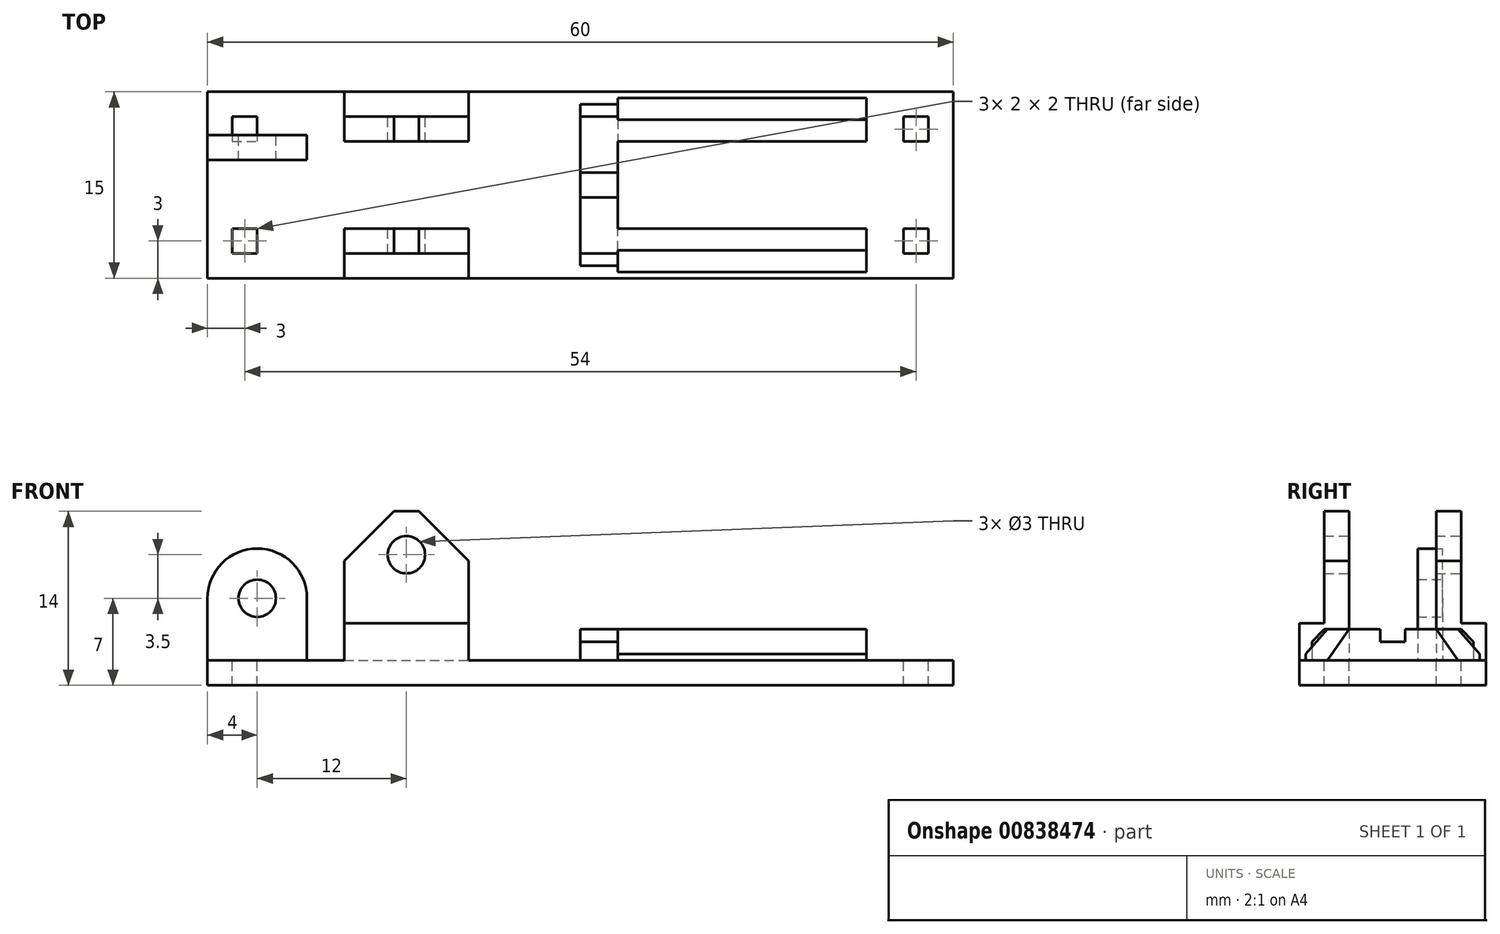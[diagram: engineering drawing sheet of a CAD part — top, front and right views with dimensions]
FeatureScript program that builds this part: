
annotation { "Feature Type Name" : "Feature", "Feature Type Description" : "" }
export const myFeature = defineFeature(function(context is Context, id is Id, definition is map)
    precondition{}
    {
        {
            var Q0;
            Q0=qCreatedBy(makeId("Top.planeOp"),FACE);
            var sketch = newSketch(context, id + "F0", { "sketchPlane" : qUnion([Q0])});
            skLineSegment(sketch, "E0.bottom", {"start": v(-30, -7.5) * mm, "end": v(30, -7.5) * mm});
            skLineSegment(sketch, "E0.top", {"start": v(-30, 7.5) * mm, "end": v(30, 7.5) * mm});
            skLineSegment(sketch, "E0.left", {"start": v(-30, -7.5) * mm, "end": v(-30, 7.5) * mm});
            skLineSegment(sketch, "E0.right", {"start": v(30, -7.5) * mm, "end": v(30, 7.5) * mm});
            skPoint(sketch, "E0.middle", {"position": v(0, 0) * mm});
            skLineSegment(sketch, "E1.bottom", {"start": v(-28, 5.5) * mm, "end": v(-26, 5.5) * mm});
            skLineSegment(sketch, "E1.top", {"start": v(-28, 3.5) * mm, "end": v(-26, 3.5) * mm});
            skLineSegment(sketch, "E1.left", {"start": v(-28, 5.5) * mm, "end": v(-28, 3.5) * mm});
            skLineSegment(sketch, "E1.right", {"start": v(-26, 5.5) * mm, "end": v(-26, 3.5) * mm});
            skLineSegment(sketch, "E2.bottom", {"start": v(-28, -3.5) * mm, "end": v(-26, -3.5) * mm});
            skLineSegment(sketch, "E2.top", {"start": v(-28, -5.5) * mm, "end": v(-26, -5.5) * mm});
            skLineSegment(sketch, "E2.left", {"start": v(-28, -3.5) * mm, "end": v(-28, -5.5) * mm});
            skLineSegment(sketch, "E2.right", {"start": v(-26, -3.5) * mm, "end": v(-26, -5.5) * mm});
            skLineSegment(sketch, "E3.bottom", {"start": v(26, -3.5) * mm, "end": v(28, -3.5) * mm});
            skLineSegment(sketch, "E3.top", {"start": v(26, -5.5) * mm, "end": v(28, -5.5) * mm});
            skLineSegment(sketch, "E3.left", {"start": v(26, -3.5) * mm, "end": v(26, -5.5) * mm});
            skLineSegment(sketch, "E3.right", {"start": v(28, -3.5) * mm, "end": v(28, -5.5) * mm});
            skLineSegment(sketch, "E4.bottom", {"start": v(26, 3.5) * mm, "end": v(28, 3.5) * mm});
            skLineSegment(sketch, "E4.top", {"start": v(26, 5.5) * mm, "end": v(28, 5.5) * mm});
            skLineSegment(sketch, "E4.left", {"start": v(26, 3.5) * mm, "end": v(26, 5.5) * mm});
            skLineSegment(sketch, "E4.right", {"start": v(28, 3.5) * mm, "end": v(28, 5.5) * mm});
            skLineSegment(sketch, "E5.bottom", {"start": v(-19, 5.5) * mm, "end": v(-9, 5.5) * mm});
            skLineSegment(sketch, "E5.top", {"start": v(-19, 3.5) * mm, "end": v(-9, 3.5) * mm});
            skLineSegment(sketch, "E5.left", {"start": v(-19, 5.5) * mm, "end": v(-19, 3.5) * mm});
            skLineSegment(sketch, "E5.right", {"start": v(-9, 5.5) * mm, "end": v(-9, 3.5) * mm});
            skLineSegment(sketch, "E6.bottom", {"start": v(-19, -3.5) * mm, "end": v(-9, -3.5) * mm});
            skLineSegment(sketch, "E6.top", {"start": v(-19, -5.5) * mm, "end": v(-9, -5.5) * mm});
            skLineSegment(sketch, "E6.left", {"start": v(-19, -3.5) * mm, "end": v(-19, -5.5) * mm});
            skLineSegment(sketch, "E6.right", {"start": v(-9, -3.5) * mm, "end": v(-9, -5.5) * mm});
            skLineSegment(sketch, "E7", {"start": v(-9, -5.5) * mm, "end": v(-9, -7.5) * mm});
            skLineSegment(sketch, "E8", {"start": v(-19, -5.5) * mm, "end": v(-19, -7.5) * mm});
            skLineSegment(sketch, "E9", {"start": v(-19, 5.5) * mm, "end": v(-19, 7.5) * mm});
            skLineSegment(sketch, "E10", {"start": v(-9, 5.5) * mm, "end": v(-9, 7.5) * mm});
            skLineSegment(sketch, "E11.bottom", {"start": v(3, -3.5) * mm, "end": v(23, -3.5) * mm});
            skLineSegment(sketch, "E11.top", {"start": v(3, -7) * mm, "end": v(23, -7) * mm});
            skLineSegment(sketch, "E11.left", {"start": v(3, -3.5) * mm, "end": v(3, -7) * mm});
            skLineSegment(sketch, "E11.right", {"start": v(23, -3.5) * mm, "end": v(23, -7) * mm});
            skLineSegment(sketch, "E12.bottom", {"start": v(3, 7) * mm, "end": v(23, 7) * mm});
            skLineSegment(sketch, "E12.top", {"start": v(3, 3.5) * mm, "end": v(23, 3.5) * mm});
            skLineSegment(sketch, "E12.left", {"start": v(3, 7) * mm, "end": v(3, 3.5) * mm});
            skLineSegment(sketch, "E12.right", {"start": v(23, 7) * mm, "end": v(23, 3.5) * mm});
            skLineSegment(sketch, "E13.bottom", {"start": v(3, 6.5) * mm, "end": v(0, 6.5) * mm});
            skLineSegment(sketch, "E13.top", {"start": v(3, -6.5) * mm, "end": v(0, -6.5) * mm});
            skLineSegment(sketch, "E13.left", {"start": v(3, 6.5) * mm, "end": v(3, -6.5) * mm});
            skLineSegment(sketch, "E13.right", {"start": v(0, 6.5) * mm, "end": v(0, -6.5) * mm});
            skSolve(sketch);
        }
        {
            var Q0;
            {var subQ0=sQuery(id+"F0.wireOp",EDGE,"E0.left");Q0=qUnion([makeQuery(id+"F0.imprint","IMPRINT",FACE,{"disambiguationData":[TD([[makeQuery(id+"F0.imprint","IMPRINT",EDGE,{"derivedFrom":sQuery(id+"F0.wireOp",EDGE,"E6.top")}),-1.0]])]}),makeQuery(id+"F0.imprint","IMPRINT",FACE,{"disambiguationData":[TD([[makeQuery(id+"F0.imprint","IMPRINT",EDGE,{"derivedFrom":sQuery(id+"F0.wireOp",EDGE,"E5.bottom")}),1.0]])]}),makeQuery(id+"F0.imprint","IMPRINT",FACE,{"disambiguationData":[TD([[makeQuery(id+"F0.imprint","IMPRINT",EDGE,{"derivedFrom":subQ0}),-1.0]])]})]);}
            var Q1;
            Q1=makeQuery(id+"F0.imprint","IMPRINT",FACE,{"disambiguationData":[TD([[makeQuery(id+"F0.imprint","IMPRINT",EDGE,{"derivedFrom":sQuery(id+"F0.wireOp",EDGE,"E5.bottom")}),-1.0]])]});
            var Q2;
            Q2=makeQuery(id+"F0.imprint","IMPRINT",FACE,{"disambiguationData":[TD([[makeQuery(id+"F0.imprint","IMPRINT",EDGE,{"derivedFrom":sQuery(id+"F0.wireOp",EDGE,"E6.bottom")}),-1.0]])]});
            var Q3;
            {var subQ1=sQuery(id+"F0.wireOp",EDGE,"E12.bottom");Q3=makeQuery(id+"F0.imprint","IMPRINT",FACE,{"disambiguationData":[TD([[makeQuery(id+"F0.imprint","IMPRINT",EDGE,{"derivedFrom":subQ1}),-1.0]])]});}
            var Q4;
            {var subQ3=sQuery(id+"F0.wireOp",EDGE,"E11.bottom");Q4=makeQuery(id+"F0.imprint","IMPRINT",FACE,{"disambiguationData":[TD([[makeQuery(id+"F0.imprint","IMPRINT",EDGE,{"derivedFrom":subQ3}),-1.0]])]});}
            var Q5;
            {var subQ1=sQuery(id+"F0.wireOp",EDGE,"E13.bottom");Q5=makeQuery(id+"F0.imprint","IMPRINT",FACE,{"disambiguationData":[TD([[makeQuery(id+"F0.imprint","IMPRINT",EDGE,{"derivedFrom":subQ1}),1.0]])]});}
            extrude(context, id + "F1", {"entities" : qUnion([Q0, Q1, Q2, Q3, Q4, Q5]), "oppositeDirection" : true, "depth" : 2 * mm, "offsetDistance" : 25 * mm});
        }
        {
            var Q0;
            Q0=makeQuery(id+"F0.imprint","IMPRINT",FACE,{"disambiguationData":[TD([[makeQuery(id+"F0.imprint","IMPRINT",EDGE,{"derivedFrom":sQuery(id+"F0.wireOp",EDGE,"E5.bottom")}),-1.0]])]});
            var Q1;
            Q1=makeQuery(id+"F0.imprint","IMPRINT",FACE,{"disambiguationData":[TD([[makeQuery(id+"F0.imprint","IMPRINT",EDGE,{"derivedFrom":sQuery(id+"F0.wireOp",EDGE,"E6.bottom")}),-1.0]])]});
            extrude(context, id + "F2", {"entities" : qUnion([Q0, Q1]), "operationType" : NewBodyOperationType.ADD, "depth" : 12 * mm, "offsetDistance" : 25 * mm});
        }
        {
            var Q0;
            Q0=makeQuery(id+"F2.opExtrude","SWEPT_FACE",FACE,{"disambiguationData":[OSD([sQuery(id+"F0.wireOp",EDGE,"E5.bottom")])]});
            var sketch = newSketch(context, id + "F3", { "sketchPlane" : qUnion([Q0])});
            skCircle(sketch, "E14", {"center": v(14, 8.5) * mm, "radius": 1.5 * mm});
            skLineSegment(sketch, "E15", {"start": v(14, 0) * mm, "end": v(14, 17) * mm});
            skSolve(sketch);
        }
        {
            var Q0;
            {var subQ0=sQuery(id+"F3.wireOp",EDGE,"E15");var subQ1=sQuery(id+"F3.wireOp",EDGE,"E14");var subQ2=makeQuery(id+"F3.imprint","INTERSECT",VERTEX,{"disambiguationData":[OD(0.0)],"derivedFrom":[subQ1,subQ0]});Q0=makeQuery(id+"F3.imprint","IMPRINT",FACE,{"disambiguationData":[TD([[makeQuery(id+"F3.imprint","IMPRINT",EDGE,{"disambiguationData":[TD([[subQ2,-1.0]])],"derivedFrom":subQ1}),1.0]])]});}
            var Q1;
            {var subQ0=sQuery(id+"F3.wireOp",EDGE,"E15");var subQ1=sQuery(id+"F3.wireOp",EDGE,"E14");var subQ2=makeQuery(id+"F3.imprint","INTERSECT",VERTEX,{"disambiguationData":[OD(0.0)],"derivedFrom":[subQ1,subQ0]});Q1=makeQuery(id+"F3.imprint","IMPRINT",FACE,{"disambiguationData":[TD([[makeQuery(id+"F3.imprint","IMPRINT",EDGE,{"disambiguationData":[TD([[subQ2,1.0]])],"derivedFrom":subQ1}),1.0]])]});}
            extrude(context, id + "F4", {"entities" : qUnion([Q0, Q1]), "operationType" : NewBodyOperationType.REMOVE, "oppositeDirection" : true, "depth" : 25 * mm, "offsetDistance" : 25 * mm});
        }
        {
            var Q0;
            Q0=makeQuery(id+"F0.imprint","IMPRINT",FACE,{"disambiguationData":[TD([[makeQuery(id+"F0.imprint","IMPRINT",EDGE,{"derivedFrom":sQuery(id+"F0.wireOp",EDGE,"E5.bottom")}),1.0]])]});
            var Q1;
            Q1=makeQuery(id+"F0.imprint","IMPRINT",FACE,{"disambiguationData":[TD([[makeQuery(id+"F0.imprint","IMPRINT",EDGE,{"derivedFrom":sQuery(id+"F0.wireOp",EDGE,"E6.top")}),-1.0]])]});
            extrude(context, id + "F5", {"entities" : qUnion([Q0, Q1]), "operationType" : NewBodyOperationType.ADD, "depth" : 3 * mm, "offsetDistance" : 25 * mm});
        }
        {
            var Q0;
            Q0=qCreatedBy(makeId("Front.planeOp"),FACE);
            cPlane(context, id + "F6", {"entities" : qUnion([Q0]), "cplaneType" : CPlaneType.OFFSET, "offset" : 3 * mm, "oppositeDirection" : true, "width" : 150 * mm, "height" : 150 * mm});
        }
        {
            var Q0;
            Q0=qCreatedBy(id+"F6.planeOp",FACE);
            var sketch = newSketch(context, id + "F7", { "sketchPlane" : qUnion([Q0])});
            skPoint(sketch, "E16.0", {"position": v(-30, 0) * mm});
            skPoint(sketch, "E16.1", {"position": v(-19, 0) * mm});
            skCircle(sketch, "E17", {"center": v(-26, 5) * mm, "radius": 1.5 * mm});
            skCircle(sketch, "E18", {"center": v(-26, 5) * mm, "radius": 4 * mm});
            skLineSegment(sketch, "E19", {"start": v(-19, 0) * mm, "end": v(-30, 0) * mm});
            skLineSegment(sketch, "E20", {"start": v(-22, 5) * mm, "end": v(-22, 0) * mm});
            skLineSegment(sketch, "E21", {"start": v(-30, 5) * mm, "end": v(-30, 0) * mm});
            skSolve(sketch);
        }
        {
            var Q0;
            Q0=makeQuery(id+"F7.imprint","IMPRINT",FACE,{"disambiguationData":[TD([[makeQuery(id+"F7.imprint","IMPRINT",EDGE,{"derivedFrom":sQuery(id+"F7.wireOp",EDGE,"E17")}),-1.0]])]});
            var Q1;
            {var subQ0=sQuery(id+"F7.wireOp",EDGE,"E20");Q1=makeQuery(id+"F7.imprint","IMPRINT",FACE,{"disambiguationData":[TD([[makeQuery(id+"F7.imprint","IMPRINT",EDGE,{"derivedFrom":subQ0}),-1.0]])]});}
            extrude(context, id + "F8", {"entities" : qUnion([Q0, Q1]), "operationType" : NewBodyOperationType.ADD, "depth" : 2 * mm, "offsetDistance" : 25 * mm, "symmetric" : true});
        }
        {
            var Q0;
            Q0=makeQuery(id+"F2.opExtrude","CAP_EDGE",EDGE,{"disambiguationData":[OSD([sQuery(id+"F0.wireOp",EDGE,"E5.right")])],"isStart":false});
            var Q1;
            Q1=makeQuery(id+"F2.opExtrude","CAP_EDGE",EDGE,{"disambiguationData":[OSD([sQuery(id+"F0.wireOp",EDGE,"E5.left")])],"isStart":false});
            chamfer(context, id + "F9", {"entities" : qUnion([Q0, Q1]), "width" : 4 * mm, "tangentPropagation" : true});
        }
        {
            var Q0;
            Q0=makeQuery(id+"F2.opExtrude","CAP_EDGE",EDGE,{"disambiguationData":[OSD([sQuery(id+"F0.wireOp",EDGE,"E6.right")])],"isStart":false});
            var Q1;
            Q1=makeQuery(id+"F2.opExtrude","CAP_EDGE",EDGE,{"disambiguationData":[OSD([sQuery(id+"F0.wireOp",EDGE,"E6.left")])],"isStart":false});
            chamfer(context, id + "F10", {"entities" : qUnion([Q0, Q1]), "width" : 4 * mm, "tangentPropagation" : true});
        }
        {
            var Q0;
            {var subQ3=sQuery(id+"F0.wireOp",EDGE,"E11.bottom");Q0=makeQuery(id+"F0.imprint","IMPRINT",FACE,{"disambiguationData":[TD([[makeQuery(id+"F0.imprint","IMPRINT",EDGE,{"derivedFrom":subQ3}),-1.0]])]});}
            var Q1;
            {var subQ1=sQuery(id+"F0.wireOp",EDGE,"E12.bottom");Q1=makeQuery(id+"F0.imprint","IMPRINT",FACE,{"disambiguationData":[TD([[makeQuery(id+"F0.imprint","IMPRINT",EDGE,{"derivedFrom":subQ1}),-1.0]])]});}
            var Q2;
            {var subQ1=sQuery(id+"F0.wireOp",EDGE,"E13.bottom");Q2=makeQuery(id+"F0.imprint","IMPRINT",FACE,{"disambiguationData":[TD([[makeQuery(id+"F0.imprint","IMPRINT",EDGE,{"derivedFrom":subQ1}),1.0]])]});}
            extrude(context, id + "F11", {"entities" : qUnion([Q0, Q1, Q2]), "operationType" : NewBodyOperationType.ADD, "depth" : 2.5 * mm, "offsetDistance" : 25 * mm});
        }
        {
            var Q0;
            Q0=makeQuery(id+"F11.opExtrude","SWEPT_FACE",FACE,{"disambiguationData":[OSD([sQuery(id+"F0.wireOp",EDGE,"E11.right")])]});
            var sketch = newSketch(context, id + "F12", { "sketchPlane" : qUnion([Q0])});
            skLineSegment(sketch, "E22", {"start": v(-5.25, 0) * mm, "end": v(-3.5, 2.5) * mm});
            skLineSegment(sketch, "E23", {"start": v(-3.5, 2.5) * mm, "end": v(-3.5, 0) * mm});
            skLineSegment(sketch, "E24", {"start": v(-3.5, 0) * mm, "end": v(-5.25, 0) * mm});
            skLineSegment(sketch, "E25.MirrorCS", {"start": v(3.5, 2.5) * mm, "end": v(3.5, 0) * mm});
            skLineSegment(sketch, "E26.MirrorCS", {"start": v(5.25, 0) * mm, "end": v(3.5, 2.5) * mm});
            skLineSegment(sketch, "E27.MirrorCS", {"start": v(3.5, 0) * mm, "end": v(5.25, 0) * mm});
            skLineSegment(sketch, "E28", {"start": v(-7, 2.5) * mm, "end": v(-5.25, 2.5) * mm});
            skLineSegment(sketch, "E29", {"start": v(-7, 2.5) * mm, "end": v(-7, 0.5) * mm});
            skLineSegment(sketch, "E30", {"start": v(-7, 0.5) * mm, "end": v(-5.25, 2.5) * mm});
            skLineSegment(sketch, "E31.MirrorCS", {"start": v(7, 2.5) * mm, "end": v(7, 0.5) * mm});
            skLineSegment(sketch, "E32.MirrorCS", {"start": v(7, 2.5) * mm, "end": v(5.25, 2.5) * mm});
            skLineSegment(sketch, "E33.MirrorCS", {"start": v(7, 0.5) * mm, "end": v(5.25, 2.5) * mm});
            skPoint(sketch, "E34", {"position": v(-4.2, 1.5) * mm});
            skPoint(sketch, "E35", {"position": v(4.2, 1.5) * mm});
            skSolve(sketch);
        }
        {
            var Q0;
            Q0=makeQuery(id+"F12.imprint","IMPRINT",FACE,{"disambiguationData":[TD([[makeQuery(id+"F12.imprint","IMPRINT",EDGE,{"derivedFrom":sQuery(id+"F12.wireOp",EDGE,"E22")}),-1.0]])]});
            var Q1;
            Q1=makeQuery(id+"F12.imprint","IMPRINT",FACE,{"disambiguationData":[TD([[makeQuery(id+"F12.imprint","IMPRINT",EDGE,{"derivedFrom":sQuery(id+"F12.wireOp",EDGE,"E28")}),1.0]])]});
            var Q2;
            Q2=makeQuery(id+"F12.imprint","IMPRINT",FACE,{"disambiguationData":[TD([[makeQuery(id+"F12.imprint","IMPRINT",EDGE,{"derivedFrom":sQuery(id+"F12.wireOp",EDGE,"E31.MirrorCS")}),-1.0]])]});
            var Q3;
            Q3=makeQuery(id+"F12.imprint","IMPRINT",FACE,{"disambiguationData":[TD([[makeQuery(id+"F12.imprint","IMPRINT",EDGE,{"derivedFrom":sQuery(id+"F12.wireOp",EDGE,"E25.MirrorCS")}),1.0]])]});
            extrude(context, id + "F13", {"entities" : qUnion([Q0, Q1, Q2, Q3]), "operationType" : NewBodyOperationType.REMOVE, "oppositeDirection" : true, "depth" : 20 * mm, "offsetDistance" : 25 * mm});
        }
        {
            var Q0;
            Q0=makeQuery(id+"F11.opExtrude","CAP_EDGE",EDGE,{"disambiguationData":[OSD([sQuery(id+"F0.wireOp",EDGE,"E13.bottom")])],"isStart":false});
            var Q1;
            Q1=makeQuery(id+"F11.opExtrude","CAP_EDGE",EDGE,{"disambiguationData":[OSD([sQuery(id+"F0.wireOp",EDGE,"E13.top")])],"isStart":false});
            chamfer(context, id + "F14", {"entities" : qUnion([Q0, Q1]), "width" : 1 * mm, "tangentPropagation" : true});
        }
        {
            var Q0;
            Q0=makeQuery(id+"F11.opExtrude","CAP_FACE",FACE,{"disambiguationData":[OSD([sQuery(id+"F0.wireOp",EDGE,"E11.bottom"),sQuery(id+"F0.wireOp",EDGE,"E11.top"),sQuery(id+"F0.wireOp",EDGE,"E11.left"),sQuery(id+"F0.wireOp",EDGE,"E11.right"),sQuery(id+"F0.wireOp",EDGE,"E12.bottom"),sQuery(id+"F0.wireOp",EDGE,"E12.top"),sQuery(id+"F0.wireOp",EDGE,"E12.left"),sQuery(id+"F0.wireOp",EDGE,"E12.right"),sQuery(id+"F0.wireOp",EDGE,"E13.bottom"),sQuery(id+"F0.wireOp",EDGE,"E13.top"),sQuery(id+"F0.wireOp",EDGE,"E13.left"),sQuery(id+"F0.wireOp",EDGE,"E13.right")])],"isStart":false});
            var sketch = newSketch(context, id + "F15", { "sketchPlane" : qUnion([Q0])});
            skLineSegment(sketch, "E36.bottom", {"start": v(0, 1) * mm, "end": v(3, 1) * mm});
            skLineSegment(sketch, "E36.top", {"start": v(0, -1) * mm, "end": v(3, -1) * mm});
            skLineSegment(sketch, "E36.left", {"start": v(0, 1) * mm, "end": v(0, -1) * mm});
            skLineSegment(sketch, "E36.right", {"start": v(3, 1) * mm, "end": v(3, -1) * mm});
            skSolve(sketch);
        }
        {
            var Q0;
            Q0=makeQuery(id+"F15.imprint","IMPRINT",FACE,{"disambiguationData":[TD([[makeQuery(id+"F15.imprint","IMPRINT",EDGE,{"derivedFrom":sQuery(id+"F15.wireOp",EDGE,"E36.bottom")}),-1.0]])]});
            extrude(context, id + "F16", {"entities" : qUnion([Q0]), "operationType" : NewBodyOperationType.REMOVE, "oppositeDirection" : true, "depth" : 1 * mm, "offsetDistance" : 25 * mm});
        }
    });
